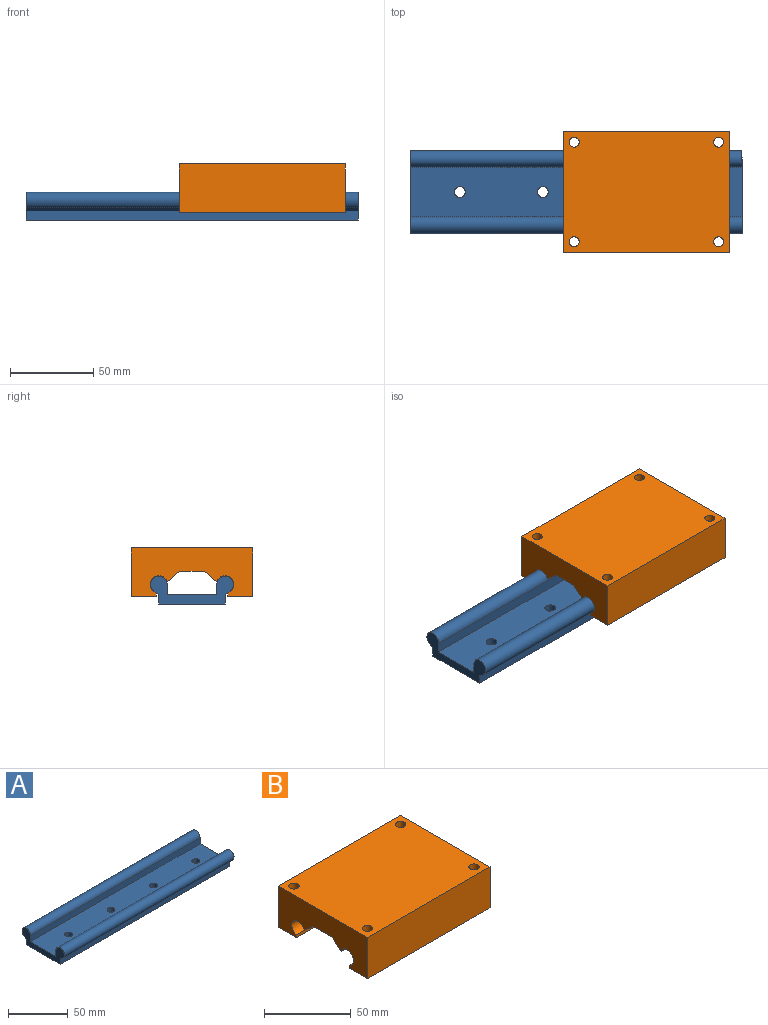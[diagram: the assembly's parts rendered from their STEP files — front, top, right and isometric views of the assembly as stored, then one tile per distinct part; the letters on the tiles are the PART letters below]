
ASSEMBLY  parts=2 mates=2
PART A: 16 faces, bbox 200x50x16.8 mm
  f0: plane 200x30mm, normal (0,0,1), area 5867.3mm2, adj f4,f5,f7,f9,f12,f13,f14,f15
  f1: plane 200x5.5mm, normal (0,1,0), area 1100mm2, adj f3,f4,f5,f10
  f2: plane 200x5.5mm, normal (0,-1,0), area 1100mm2, adj f3,f4,f5,f6
  f3: plane 200x40mm, normal (0,0,-1), area 7867.3mm2, adj f1,f2,f4,f5,f12,f13,f14,f15
  f4: plane 50x16.75mm, normal (-1,0,0), area 403mm2, adj f0,f1,f2,f3,f6,f7,f8,f9
  f5: plane 50x16.75mm, normal (1,0,0), area 403mm2, adj f0,f1,f2,f3,f6,f7,f8,f9
  f6: plane 200x3mm, normal (0,-0.6,-0.8), area 750mm2, adj f2,f4,f5,f8
  f7: plane 200x6.25mm, normal (0,1,0), area 1250mm2, adj f0,f4,f5,f8
  f8: cylinder r=5mm len=200mm, axis (1,0,0), area 4068.9mm2, adj f4,f5,f6,f7
  f9: plane 200x6.25mm, normal (0,-1,0), area 1250mm2, adj f0,f4,f5,f11
  f10: plane 200x3mm, normal (0,0.6,-0.8), area 750mm2, adj f1,f4,f5,f11
  f11: cylinder r=5mm len=200mm, axis (1,0,0), area 4068.9mm2, adj f4,f5,f9,f10
  f12: cylinder r=3.25mm len=6.5mm, axis (0,0,1), area 112.3mm2, adj f0,f3
  f13: cylinder r=3.25mm len=6.5mm, axis (0,0,1), area 112.3mm2, adj f0,f3
  f14: cylinder r=3.25mm len=6.5mm, axis (0,0,1), area 112.3mm2, adj f0,f3
  f15: cylinder r=3.25mm len=6.5mm, axis (0,0,1), area 112.3mm2, adj f0,f3
PART B: 18 faces, bbox 100x73x29 mm
  f0: plane 100x15mm, normal (0,0,-1), area 1443.5mm2, adj f1,f2,f3,f7,f10,f11
  f1: plane 73x29mm, normal (1,0,0), area 1511mm2, adj f0,f3,f4,f5,f6,f11,f12,f13
  f2: plane 73x29mm, normal (-1,0,0), area 1511mm2, adj f0,f3,f4,f5,f6,f11,f12,f13
  f3: plane 100x29mm, normal (0,1,0), area 2900mm2, adj f0,f1,f2,f5
  f4: plane 100x29mm, normal (0,-1,0), area 2900mm2, adj f1,f2,f5,f6
  f5: plane 100x73mm, normal (0,0,1), area 7186.9mm2, adj f1,f2,f3,f4,f7,f8,f9,f10
  f6: plane 100x15mm, normal (0,0,-1), area 1443.5mm2, adj f1,f2,f4,f8,f9,f17
  f7: cylinder r=3mm len=29mm, axis (0,0,1), area 546.6mm2, adj f0,f5
  f8: cylinder r=3mm len=29mm, axis (0,0,1), area 546.6mm2, adj f5,f6
  f9: cylinder r=3mm len=29mm, axis (0,0,1), area 546.6mm2, adj f5,f6
  f10: cylinder r=3mm len=29mm, axis (0,0,1), area 546.6mm2, adj f0,f5
  f11: plane 100x1.97mm, normal (0,-1,0), area 196.9mm2, adj f0,f1,f2,f12
  f12: cylinder r=5.25mm len=100mm, axis (1,0,0), area 2159.2mm2, adj f1,f2,f11,f13
  f13: plane 100x7.63mm, normal (0,-0.64,-0.77), area 995.5mm2, adj f1,f2,f12,f15
  f14: cylinder r=5.25mm len=100mm, axis (1,0,0), area 2159.2mm2, adj f1,f2,f16,f17
  f15: plane 100x14.75mm, normal (0,0,-1), area 1474.7mm2, adj f1,f2,f13,f16
  f16: plane 100x7.63mm, normal (0,0.64,-0.77), area 995.5mm2, adj f1,f2,f14,f15
  f17: plane 100x1.97mm, normal (0,1,0), area 196.9mm2, adj f1,f2,f6,f14
PLACE A t=(-37.55,-10.94,52)mm fixed
PLACE B t=(-95.15,-10.94,54)mm
MATE slider A.f8 <-> B.f14  axis (1,0,0) through (-37.55,-30.94,61)mm
MATE slider A.f11 <-> B.f12  axis (1,0,0) through (-37.55,9.06,61)mm
